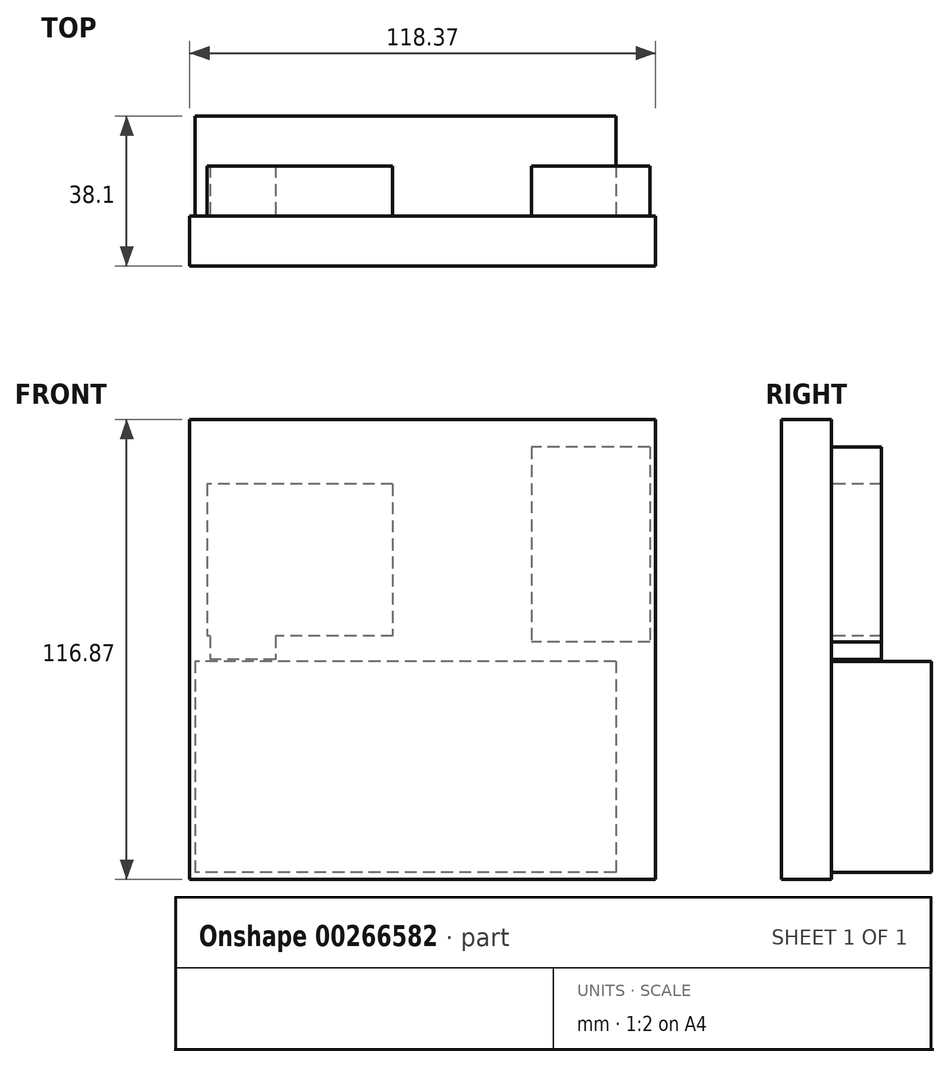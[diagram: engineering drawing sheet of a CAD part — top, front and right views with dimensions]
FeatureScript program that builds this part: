
annotation { "Feature Type Name" : "Feature", "Feature Type Description" : "" }
export const myFeature = defineFeature(function(context is Context, id is Id, definition is map)
    precondition{}
    {
        {
            var Q0;
            Q0=qCreatedBy(makeId("Front.planeOp"),FACE);
            var sketch = newSketch(context, id + "F0", { "sketchPlane" : qUnion([Q0])});
            skLineSegment(sketch, "E0.bottom", {"start": v(77.17, -55.44) * mm, "end": v(195.54, -55.44) * mm});
            skLineSegment(sketch, "E0.top", {"start": v(77.17, 61.43) * mm, "end": v(195.54, 61.43) * mm});
            skLineSegment(sketch, "E0.left", {"start": v(77.17, -55.44) * mm, "end": v(77.17, 61.43) * mm});
            skLineSegment(sketch, "E0.right", {"start": v(195.54, -55.44) * mm, "end": v(195.54, 61.43) * mm});
            skPoint(sketch, "E0.middle", {"position": v(136.35, 3) * mm});
            skSolve(sketch);
        }
        {
            var Q0;
            Q0 = qSketchRegion(id + "F0", true);
            extrude(context, id + "F1", {"entities" : qUnion([Q0]), "depth" : 12.7 * mm});
        }
        {
            var Q0;
            Q0=makeQuery(id+"F1.opExtrude","CAP_FACE",FACE,{"disambiguationData":[OSD([sQuery(id+"F0.wireOp",EDGE,"E0.bottom"),sQuery(id+"F0.wireOp",EDGE,"E0.top"),sQuery(id+"F0.wireOp",EDGE,"E0.left"),sQuery(id+"F0.wireOp",EDGE,"E0.right")])],"isStart":true});
            var sketch = newSketch(context, id + "F2", { "sketchPlane" : qUnion([Q0])});
            skLineSegment(sketch, "E1.bottom", {"start": v(-185.43, 0) * mm, "end": v(-78.45, 0) * mm});
            skLineSegment(sketch, "E1.top", {"start": v(-185.43, -53.59) * mm, "end": v(-78.45, -53.59) * mm});
            skLineSegment(sketch, "E1.left", {"start": v(-185.43, 0) * mm, "end": v(-185.43, -53.59) * mm});
            skLineSegment(sketch, "E1.right", {"start": v(-78.45, 0) * mm, "end": v(-78.45, -53.59) * mm});
            skPoint(sketch, "E1.middle", {"position": v(-131.94, -26.8) * mm});
            skSolve(sketch);
        }
        {
            var Q0;
            Q0 = qSketchRegion(id + "F2", true);
            extrude(context, id + "F3", {"entities" : qUnion([Q0]), "operationType" : NewBodyOperationType.ADD, "depth" : 25.4 * mm});
        }
        {
            var Q0;
            Q0=makeQuery(id+"F1.opExtrude","CAP_FACE",FACE,{"disambiguationData":[OSD([sQuery(id+"F0.wireOp",EDGE,"E0.bottom"),sQuery(id+"F0.wireOp",EDGE,"E0.top"),sQuery(id+"F0.wireOp",EDGE,"E0.left"),sQuery(id+"F0.wireOp",EDGE,"E0.right")])],"isStart":true});
            var sketch = newSketch(context, id + "F4", { "sketchPlane" : qUnion([Q0])});
            skLineSegment(sketch, "E2.bottom", {"start": v(-194.09, 54.42) * mm, "end": v(-164, 54.42) * mm});
            skLineSegment(sketch, "E2.top", {"start": v(-194.09, 4.9) * mm, "end": v(-164, 4.9) * mm});
            skLineSegment(sketch, "E2.left", {"start": v(-194.09, 54.42) * mm, "end": v(-194.09, 4.9) * mm});
            skLineSegment(sketch, "E2.right", {"start": v(-164, 54.42) * mm, "end": v(-164, 4.9) * mm});
            skPoint(sketch, "E2.middle", {"position": v(-179.04, 29.66) * mm});
            skLineSegment(sketch, "E3.bottom", {"start": v(-128.72, 45) * mm, "end": v(-81.5, 45) * mm});
            skLineSegment(sketch, "E3.top", {"start": v(-128.72, 6.43) * mm, "end": v(-81.5, 6.43) * mm});
            skLineSegment(sketch, "E3.left", {"start": v(-128.72, 45) * mm, "end": v(-128.72, 6.43) * mm});
            skLineSegment(sketch, "E3.right", {"start": v(-81.5, 45) * mm, "end": v(-81.5, 6.43) * mm});
            skPoint(sketch, "E3.middle", {"position": v(-105.11, 25.71) * mm});
            skSolve(sketch);
        }
        {
            var Q0;
            {var subQ7=sQuery(id+"F4.wireOp",EDGE,"E2.bottom");Q0=makeQuery(id+"F4.imprint","IMPRINT",FACE,{"disambiguationData":[TD([[makeQuery(id+"F4.imprint","IMPRINT",EDGE,{"derivedFrom":subQ7}),-1.0]])]});}
            var Q1;
            Q1=makeQuery(id+"F4.imprint","IMPRINT",FACE,{"disambiguationData":[TD([[makeQuery(id+"F4.imprint","IMPRINT",EDGE,{"derivedFrom":sQuery(id+"F4.wireOp",EDGE,"E3.bottom")}),-1.0]])]});
            extrude(context, id + "F5", {"entities" : qUnion([Q0, Q1]), "operationType" : NewBodyOperationType.ADD, "depth" : 12.7 * mm});
        }
        {
            var Q0;
            Q0=makeQuery(id+"F1.opExtrude","CAP_FACE",FACE,{"disambiguationData":[OSD([sQuery(id+"F0.wireOp",EDGE,"E0.bottom"),sQuery(id+"F0.wireOp",EDGE,"E0.top"),sQuery(id+"F0.wireOp",EDGE,"E0.left"),sQuery(id+"F0.wireOp",EDGE,"E0.right")])],"isStart":true});
            var sketch = newSketch(context, id + "F6", { "sketchPlane" : qUnion([Q0])});
            skLineSegment(sketch, "E4.bottom", {"start": v(-98.95, 42) * mm, "end": v(-82.33, 42) * mm});
            skLineSegment(sketch, "E4.top", {"start": v(-98.95, 0.4) * mm, "end": v(-82.33, 0.4) * mm});
            skLineSegment(sketch, "E4.left", {"start": v(-98.95, 42) * mm, "end": v(-98.95, 0.4) * mm});
            skLineSegment(sketch, "E4.right", {"start": v(-82.33, 42) * mm, "end": v(-82.33, 0.4) * mm});
            skPoint(sketch, "E4.middle", {"position": v(-90.64, 21.2) * mm});
            skSolve(sketch);
        }
        {
            var Q0;
            Q0 = qSketchRegion(id + "F6", true);
            extrude(context, id + "F7", {"entities" : qUnion([Q0]), "operationType" : NewBodyOperationType.ADD, "depth" : 12.7 * mm});
        }
    });
